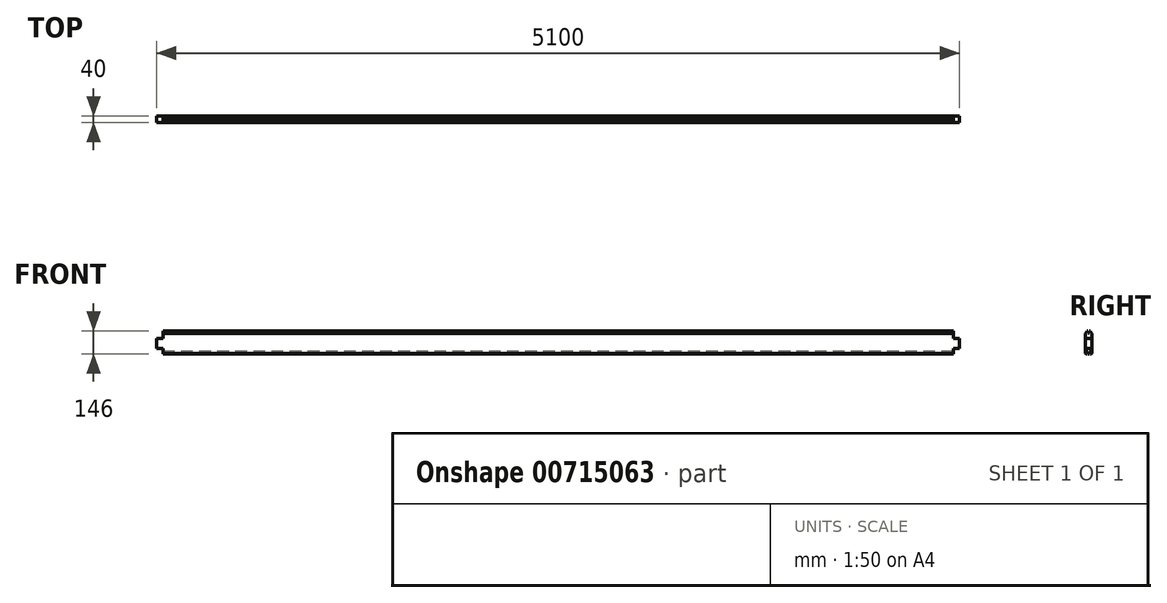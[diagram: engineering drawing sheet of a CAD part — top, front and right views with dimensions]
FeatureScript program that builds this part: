
annotation { "Feature Type Name" : "Feature", "Feature Type Description" : "" }
export const myFeature = defineFeature(function(context is Context, id is Id, definition is map)
    precondition{}
    {
        {
            assignVariable(context, id + "F0", {"name" : "Laenge", "anyValue" : 5100});
        }
        {
            var Q0;
            Q0=qCreatedBy(makeId("Right.planeOp"),FACE);
            var sketch = newSketch(context, id + "F1", { "sketchPlane" : qUnion([Q0])});
            skLineSegment(sketch, "E0", {"start": v(20, 63) * mm, "end": v(20, -63) * mm});
            skLineSegment(sketch, "E1", {"start": v(20, -63) * mm, "end": v(17, -66) * mm});
            skLineSegment(sketch, "E2", {"start": v(17, -66) * mm, "end": v(12, -66) * mm});
            skLineSegment(sketch, "E3", {"start": v(12, -52) * mm, "end": v(12, -66) * mm});
            skLineSegment(sketch, "E4", {"start": v(12, -52) * mm, "end": v(4, -52) * mm});
            skLineSegment(sketch, "E5", {"start": v(4, -66) * mm, "end": v(4, -52) * mm});
            skLineSegment(sketch, "E6", {"start": v(4, -66) * mm, "end": v(-4, -66) * mm});
            skLineSegment(sketch, "E7", {"start": v(-4, -52) * mm, "end": v(-4, -66) * mm});
            skLineSegment(sketch, "E8", {"start": v(-4, -52) * mm, "end": v(-12, -52) * mm});
            skLineSegment(sketch, "E9", {"start": v(-12, -66) * mm, "end": v(-12, -52) * mm});
            skLineSegment(sketch, "E10", {"start": v(-12, -66) * mm, "end": v(-17, -66) * mm});
            skLineSegment(sketch, "E11", {"start": v(-17, -66) * mm, "end": v(-20, -63) * mm});
            skLineSegment(sketch, "E12", {"start": v(-20, -63) * mm, "end": v(-20, 63) * mm});
            skLineSegment(sketch, "E13", {"start": v(-20, 63) * mm, "end": v(-17, 66) * mm});
            skLineSegment(sketch, "E14", {"start": v(-17, 66) * mm, "end": v(-12, 66) * mm});
            skLineSegment(sketch, "E15", {"start": v(-4, 66) * mm, "end": v(4, 66) * mm});
            skLineSegment(sketch, "E16", {"start": v(12, 66) * mm, "end": v(17, 66) * mm});
            skLineSegment(sketch, "E17", {"start": v(17, 66) * mm, "end": v(20, 63) * mm});
            skPoint(sketch, "E18.end.orphan", {"position": v(12, 57.8) * mm});
            skPoint(sketch, "E19.end.orphan", {"position": v(4, 66.3) * mm});
            skPoint(sketch, "E20.end.orphan", {"position": v(-4, 66.3) * mm});
            skLineSegment(sketch, "E21", {"start": v(-12, 66) * mm, "end": v(-12, 80) * mm});
            skLineSegment(sketch, "E22", {"start": v(-12, 80) * mm, "end": v(-4, 80) * mm});
            skLineSegment(sketch, "E23", {"start": v(-4, 80) * mm, "end": v(-4, 66) * mm});
            skLineSegment(sketch, "E24", {"start": v(4, 66) * mm, "end": v(4, 80) * mm});
            skLineSegment(sketch, "E25", {"start": v(4, 80) * mm, "end": v(12, 80) * mm});
            skLineSegment(sketch, "E26", {"start": v(12, 80) * mm, "end": v(12, 66) * mm});
            skLineSegment(sketch, "E27", {"start": v(20, -33) * mm, "end": v(-20, -33) * mm});
            skLineSegment(sketch, "E28", {"start": v(20, 33) * mm, "end": v(-20, 33) * mm});
            skPoint(sketch, "E29.end.orphan", {"position": v(-141.42, 0) * mm});
            skLineSegment(sketch, "E30", {"start": v(20, 0) * mm, "end": v(-20, 0) * mm});
            skLineSegment(sketch, "E31", {"start": v(20, 0) * mm, "end": v(-20, 0) * mm, "construction": true});
            skLineSegment(sketch, "E32", {"start": v(0, 33) * mm, "end": v(0, -33) * mm, "construction": true});
            skSolve(sketch);
        }
        {
            var Q0;
            Q0=qCreatedBy(makeId("Front.planeOp"),FACE);
            var sketch = newSketch(context, id + "F2", { "sketchPlane" : qUnion([Q0])});
            skLineSegment(sketch, "E33", {"start": v(2550, 0) * mm, "end": v(-2550, 0) * mm, "construction": true});
            skPoint(sketch, "E34.right.start.orphan", {"position": v(-259.12, 108.1) * mm});
            skPoint(sketch, "E35.left.start.orphan", {"position": v(237.35, 108.1) * mm});
            skPoint(sketch, "E36.left.end.orphan", {"position": v(237.35, -84.05) * mm});
            skPoint(sketch, "E36.bottom.start.orphan", {"position": v(237.35, -117.05) * mm});
            skPoint(sketch, "E37.right.start.orphan", {"position": v(-259.12, -117.05) * mm});
            skPoint(sketch, "E37.top.end.orphan", {"position": v(-259.12, -84.05) * mm});
            skLineSegment(sketch, "E38.bottom", {"start": v(-2590, 33) * mm, "end": v(-2510, 33) * mm});
            skLineSegment(sketch, "E38.top", {"start": v(-2590, 133) * mm, "end": v(-2510, 133) * mm});
            skLineSegment(sketch, "E38.left", {"start": v(-2590, 33) * mm, "end": v(-2590, 133) * mm});
            skLineSegment(sketch, "E38.right", {"start": v(-2510, 33) * mm, "end": v(-2510, 133) * mm});
            skPoint(sketch, "E38.middle", {"position": v(-2550, 83) * mm});
            skLineSegment(sketch, "E39.bottom", {"start": v(-2590, -133) * mm, "end": v(-2510, -133) * mm});
            skLineSegment(sketch, "E39.top", {"start": v(-2590, -33) * mm, "end": v(-2510, -33) * mm});
            skLineSegment(sketch, "E39.left", {"start": v(-2590, -133) * mm, "end": v(-2590, -33) * mm});
            skLineSegment(sketch, "E39.right", {"start": v(-2510, -133) * mm, "end": v(-2510, -33) * mm});
            skPoint(sketch, "E39.middle", {"position": v(-2550, -83) * mm});
            skLineSegment(sketch, "E40.bottom", {"start": v(2590, 33) * mm, "end": v(2510, 33) * mm});
            skLineSegment(sketch, "E40.top", {"start": v(2590, 133) * mm, "end": v(2510, 133) * mm});
            skLineSegment(sketch, "E40.left", {"start": v(2590, 33) * mm, "end": v(2590, 133) * mm});
            skLineSegment(sketch, "E40.right", {"start": v(2510, 33) * mm, "end": v(2510, 133) * mm});
            skPoint(sketch, "E40.middle", {"position": v(2550, 83) * mm});
            skLineSegment(sketch, "E41.bottom", {"start": v(2590, -33) * mm, "end": v(2510, -33) * mm});
            skLineSegment(sketch, "E41.top", {"start": v(2590, -133) * mm, "end": v(2510, -133) * mm});
            skLineSegment(sketch, "E41.left", {"start": v(2590, -33) * mm, "end": v(2590, -133) * mm});
            skLineSegment(sketch, "E41.right", {"start": v(2510, -33) * mm, "end": v(2510, -133) * mm});
            skPoint(sketch, "E41.middle", {"position": v(2550, -83) * mm});
            skSolve(sketch);
        }
        {
            var Q0;
            {var subQ3=sQuery(id+"F1.wireOp",EDGE,"E13");Q0=makeQuery(id+"F1.imprint","IMPRINT",FACE,{"disambiguationData":[TD([[makeQuery(id+"F1.imprint","IMPRINT",EDGE,{"derivedFrom":subQ3}),-1.0]])]});}
            var Q1;
            {var subQ0=sQuery(id+"F1.wireOp",EDGE,"E28");Q1=makeQuery(id+"F1.imprint","IMPRINT",FACE,{"disambiguationData":[TD([[makeQuery(id+"F1.imprint","IMPRINT",EDGE,{"derivedFrom":subQ0}),1.0]])]});}
            var Q2;
            {var subQ0=sQuery(id+"F1.wireOp",EDGE,"E27");Q2=makeQuery(id+"F1.imprint","IMPRINT",FACE,{"disambiguationData":[TD([[makeQuery(id+"F1.imprint","IMPRINT",EDGE,{"derivedFrom":subQ0}),-1.0]])]});}
            var Q3;
            {var subQ1=sQuery(id+"F1.wireOp",EDGE,"E1");Q3=makeQuery(id+"F1.imprint","IMPRINT",FACE,{"disambiguationData":[TD([[makeQuery(id+"F1.imprint","IMPRINT",EDGE,{"derivedFrom":subQ1}),-1.0]])]});}
            extrude(context, id + "F3", {"entities" : qUnion([Q0, Q1, Q2, Q3]), "endBound" : BoundingType.SYMMETRIC, "depth" : getVariable(context, 'Laenge') * mm, "offsetDistance" : 25 * mm});
        }
        {
            var Q0;
            Q0=makeQuery(id+"F2.imprint","IMPRINT",FACE,{"disambiguationData":[TD([[makeQuery(id+"F2.imprint","IMPRINT",EDGE,{"derivedFrom":sQuery(id+"F2.wireOp",EDGE,"E38.bottom")}),1.0]])]});
            var Q1;
            Q1=makeQuery(id+"F2.imprint","IMPRINT",FACE,{"disambiguationData":[TD([[makeQuery(id+"F2.imprint","IMPRINT",EDGE,{"derivedFrom":sQuery(id+"F2.wireOp",EDGE,"E39.bottom")}),1.0]])]});
            var Q2;
            Q2=makeQuery(id+"F2.imprint","IMPRINT",FACE,{"disambiguationData":[TD([[makeQuery(id+"F2.imprint","IMPRINT",EDGE,{"derivedFrom":sQuery(id+"F2.wireOp",EDGE,"E40.bottom")}),-1.0]])]});
            var Q3;
            Q3=makeQuery(id+"F2.imprint","IMPRINT",FACE,{"disambiguationData":[TD([[makeQuery(id+"F2.imprint","IMPRINT",EDGE,{"derivedFrom":sQuery(id+"F2.wireOp",EDGE,"E41.bottom")}),1.0]])]});
            extrude(context, id + "F4", {"entities" : qUnion([Q0, Q1, Q2, Q3]), "operationType" : NewBodyOperationType.REMOVE, "endBound" : BoundingType.SYMMETRIC, "depth" : 50 * mm, "offsetDistance" : 25 * mm});
        }
    });
